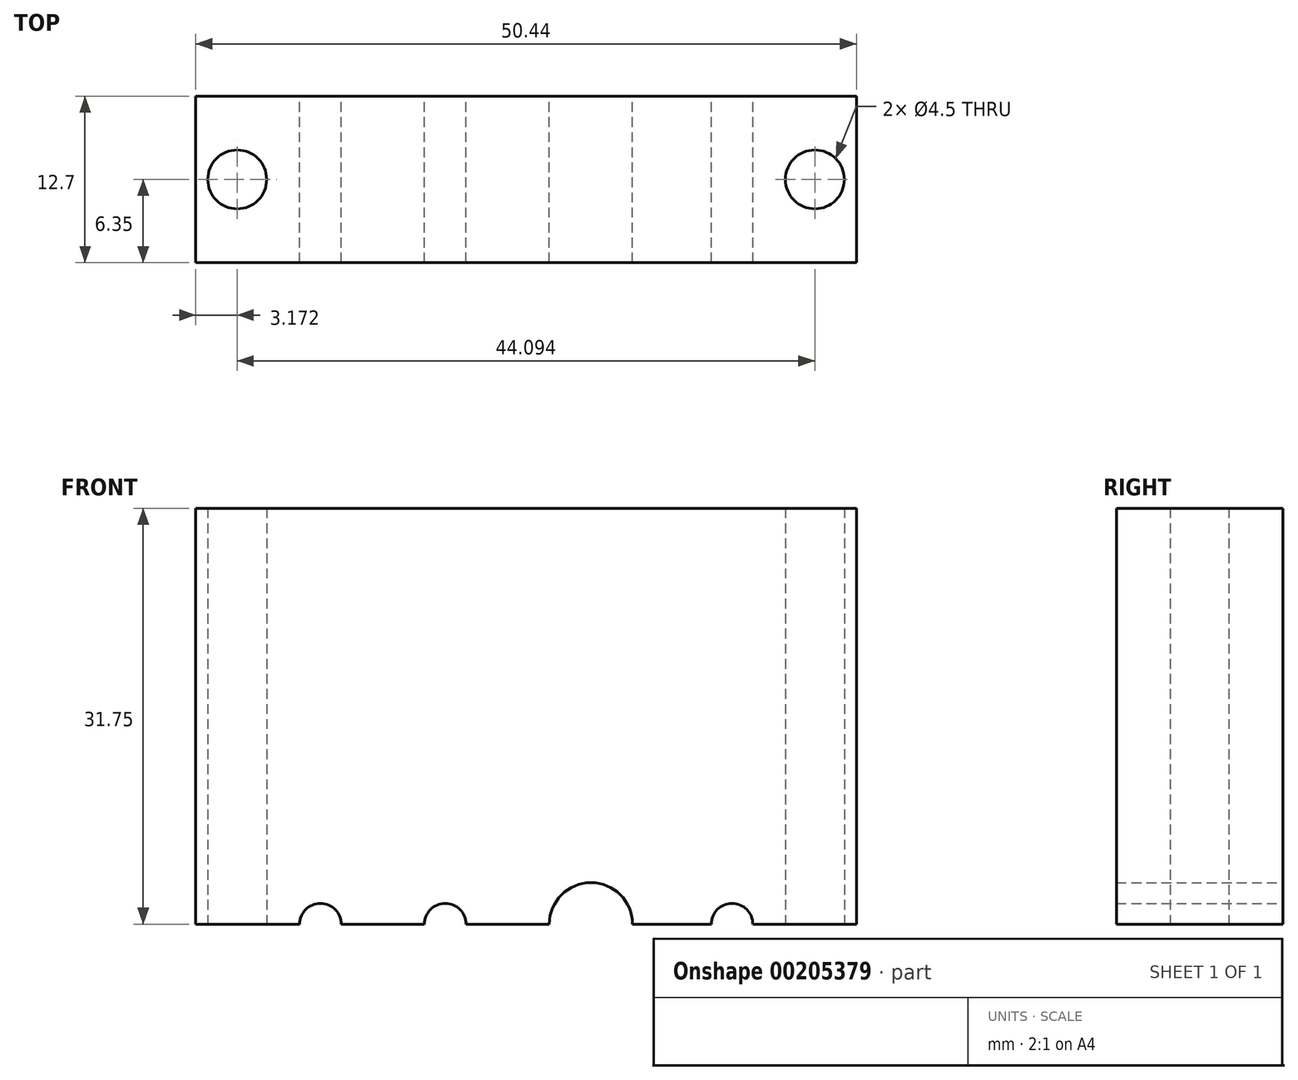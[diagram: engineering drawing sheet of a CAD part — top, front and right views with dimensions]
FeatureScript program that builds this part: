
annotation { "Feature Type Name" : "Feature", "Feature Type Description" : "" }
export const myFeature = defineFeature(function(context is Context, id is Id, definition is map)
    precondition{}
    {
        {
            var Q0;
            Q0=qCreatedBy(makeId("Front.planeOp"),FACE);
            var sketch = newSketch(context, id + "F0", { "sketchPlane" : qUnion([Q0])});
            skLineSegment(sketch, "E0.bottom", {"start": v(-51.86, -35.23) * mm, "end": v(-43.93, -35.23) * mm});
            skLineSegment(sketch, "E0.top", {"start": v(-51.86, -3.48) * mm, "end": v(-1.42, -3.48) * mm});
            skLineSegment(sketch, "E0.left", {"start": v(-51.86, -35.23) * mm, "end": v(-51.86, -3.48) * mm});
            skLineSegment(sketch, "E0.right", {"start": v(-1.42, -35.23) * mm, "end": v(-1.42, -3.48) * mm});
            skPoint(sketch, "E1", {"position": v(-42.34, -35.23) * mm});
            skPoint(sketch, "E2", {"position": v(-32.81, -35.23) * mm});
            skPoint(sketch, "E3", {"position": v(-21.69, -35.23) * mm});
            skPoint(sketch, "E4", {"position": v(-10.92, -35.23) * mm});
            skArc(sketch, "E5", {"start": v(-40.75, -35.23) * mm, "mid": v(-42.34, -33.64) * mm, "end": v(-43.93, -35.23) * mm});
            skArc(sketch, "E6", {"start": v(-31.23, -35.23) * mm, "mid": v(-32.81, -33.64) * mm, "end": v(-34.4, -35.23) * mm});
            skArc(sketch, "E7", {"start": v(-18.51, -35.23) * mm, "mid": v(-21.69, -32.06) * mm, "end": v(-24.86, -35.23) * mm});
            skArc(sketch, "E8", {"start": v(-9.33, -35.23) * mm, "mid": v(-10.92, -33.64) * mm, "end": v(-12.5, -35.23) * mm});
            skLineSegment(sketch, "E9.trimOffspring", {"start": v(-40.75, -35.23) * mm, "end": v(-34.4, -35.23) * mm});
            skLineSegment(sketch, "E10.trimOffspring", {"start": v(-31.23, -35.23) * mm, "end": v(-24.86, -35.23) * mm});
            skLineSegment(sketch, "E11.trimOffspring", {"start": v(-18.51, -35.23) * mm, "end": v(-12.5, -35.23) * mm});
            skLineSegment(sketch, "E12.trimOffspring", {"start": v(-9.33, -35.23) * mm, "end": v(-1.42, -35.23) * mm});
            skSolve(sketch);
        }
        {
            var Q0;
            Q0=makeQuery(id+"F0.imprint","IMPRINT",FACE,{"disambiguationData":[TD([[makeQuery(id+"F0.imprint","IMPRINT",EDGE,{"derivedFrom":sQuery(id+"F0.wireOp",EDGE,"E0.bottom")}),1.0]])]});
            extrude(context, id + "F1", {"entities" : qUnion([Q0]), "depth" : 12.7 * mm});
        }
        {
            var Q0;
            Q0=makeQuery(id+"F1.opExtrude","SWEPT_FACE",FACE,{"disambiguationData":[OSD([sQuery(id+"F0.wireOp",EDGE,"E0.bottom")])]});
            var sketch = newSketch(context, id + "F2", { "sketchPlane" : qUnion([Q0])});
            skPoint(sketch, "E13", {"position": v(-48.69, 6.35) * mm});
            skPoint(sketch, "E14", {"position": v(-51.86, 6.35) * mm});
            skSolve(sketch);
        }
        {
            var Q0;
            Q0=makeQuery(id+"F1.opExtrude","SWEPT_FACE",FACE,{"disambiguationData":[OSD([sQuery(id+"F0.wireOp",EDGE,"E12.trimOffspring")])]});
            var sketch = newSketch(context, id + "F3", { "sketchPlane" : qUnion([Q0])});
            skPoint(sketch, "E15", {"position": v(-4.6, 6.35) * mm});
            skPoint(sketch, "E16", {"position": v(-1.42, 6.35) * mm});
            skSolve(sketch);
        }
        {
            var Q0;
            Q0=sQuery(id+"F2.wireOp",VERTEX,"E13");
            var Q1;
            Q1=sQuery(id+"F3.wireOp",VERTEX,"E15");
            var Q2;
            Q2=makeQuery(id+"F1.opExtrude","SWEPT_BODY",BODY,{"disambiguationData":[OSD([sQuery(id+"F0.wireOp",EDGE,"E0.bottom"),sQuery(id+"F0.wireOp",EDGE,"E0.top"),sQuery(id+"F0.wireOp",EDGE,"E0.left"),sQuery(id+"F0.wireOp",EDGE,"E0.right"),sQuery(id+"F0.wireOp",EDGE,"E5"),sQuery(id+"F0.wireOp",EDGE,"E6"),sQuery(id+"F0.wireOp",EDGE,"E7"),sQuery(id+"F0.wireOp",EDGE,"E8"),sQuery(id+"F0.wireOp",EDGE,"E9.trimOffspring"),sQuery(id+"F0.wireOp",EDGE,"E10.trimOffspring"),sQuery(id+"F0.wireOp",EDGE,"E11.trimOffspring"),sQuery(id+"F0.wireOp",EDGE,"E12.trimOffspring")])]});
            hole(context, id + "F4", {"style" : HoleStyle.SIMPLE, "endStyle" : HoleEndStyle.THROUGH, "standardTappedOrClearance" : lookupTablePath({ "standard" : "ANSI", "fit" : "Normal (ASME)", "size" : "#8", "type" : "Clearance" }), "standardBlindInLast" : lookupTablePath({ "fit" : "Free", "standard" : "ANSI", "size" : "#8", "type" : "Clearance" }), "holeDiameter" : 4.5 * mm, "startFromSketch" : true, "locations" : qUnion([Q0, Q1]), "scope" : qUnion([Q2]), "isTappedThrough" : true});
        }
    });
